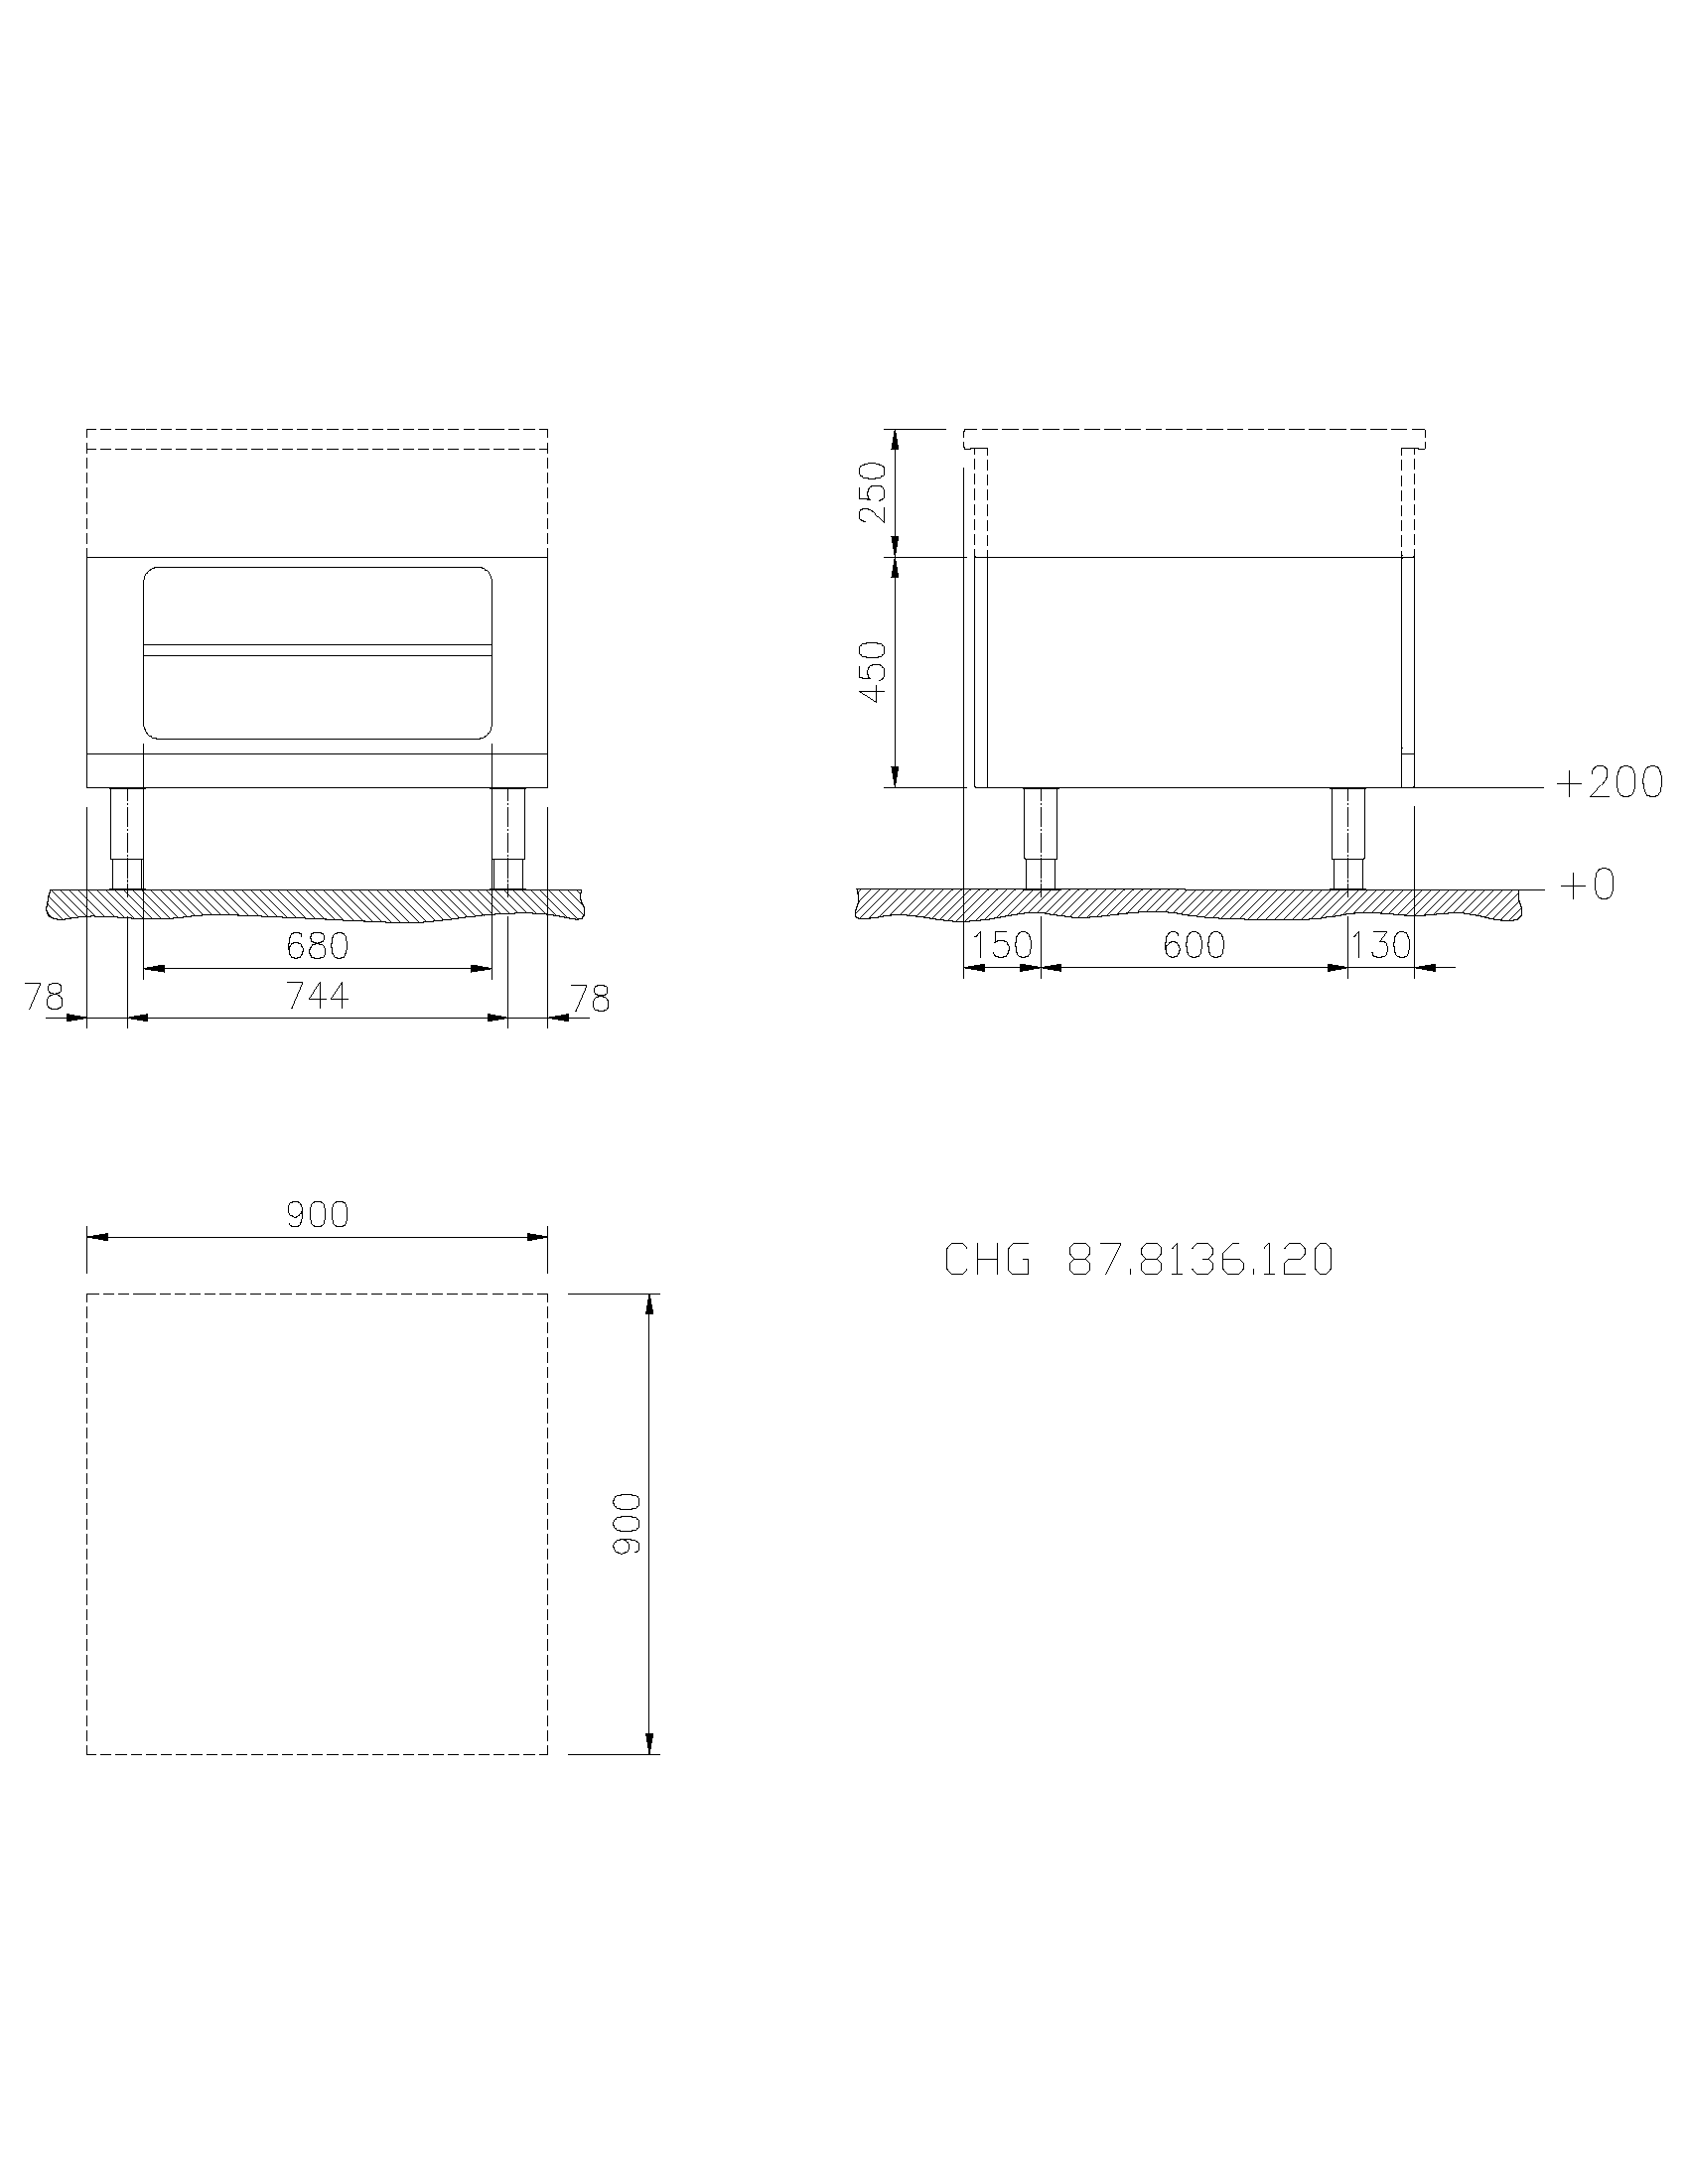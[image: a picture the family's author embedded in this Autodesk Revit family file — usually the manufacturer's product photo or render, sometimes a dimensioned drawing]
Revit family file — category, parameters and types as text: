
# Revit family: QF_ELECTROLUXPROFESSIONAL_589825_MCFAEADDDM
name_source: partatom
category: Attrezzature speciali
units: mm (PartAtom-declared; Revit-internal decimal feet)

## family parameters
Basato su piano di lavoro = No
Condiviso = No
Punto di calcolo locali = No
Quota connettore circolare = Usa diametro
Sempre verticale = Sì
Taglio con vuoti quando caricato = No
Tipo di parte = Normale

## types (1)
- Standard
    Accessory = Sì
    Cold Water Size = 0"
    Compressed Air Pressure = 0.00 psi
    Compressed Air Size = 0"
    Compressed Air Volume = 0 GPM
    Condensate Return Size = 0"
    Cycle = 50 Hz
    Depth Actual = 900 mm  [stored 2.95276 ft]
    Descrizione = DEEP FRYER,1X7L,1S,400X900X700H MARINE
    Direct Waste Size = 0"
    Gas Input Pressure = 0.0
    Gas KW = 0
    Gas Size = 0"
    HP = 7.2 HP
    Height Actual = 700 mm  [stored 2.29659 ft]
    Hot Water Size = 0"
    Item Number = 589825
    Length Actual = 400 mm  [stored 1.31234 ft]
    Modello = MCFAEADDDM
    Phase = 3
    Produttore = Electrolux Professional
    Prospetto di default = 0 mm  [stored 0 ft]
    Refrigerant Compressor Remote = Sì
    Refrigeration Liquid Line Size = 0 mm  [stored 0 ft]
    Refrigeration Suction Line Size = 0 mm  [stored 0 ft]
    Steam Consumption per Hour = 0
    Steam Supply Maximum Pressure = 0.00 psi
    Steam Supply Minimum Pressure = 0.00 psi
    Steam Supply Size = 0"
    URL = https://www.electroluxprofessional.com
    URL Manufacturer = https://www.electroluxprofessional.com
    Volts = 440 V
    Watts = 5400 W
    Weight = 70.00 kg

note: source unit labels omitted for Gas Input Pressure — the stored unit's dimension contradicts the parameter name (converter mislabeling)

note: [stored X ft] marks values corroborated as IEEE doubles in the binary element streams (Revit-internal decimal feet)

## geometry (parser evidence)
native form markers: Blend x4, Sweep x12
no freeform markers — native parametric forms only
